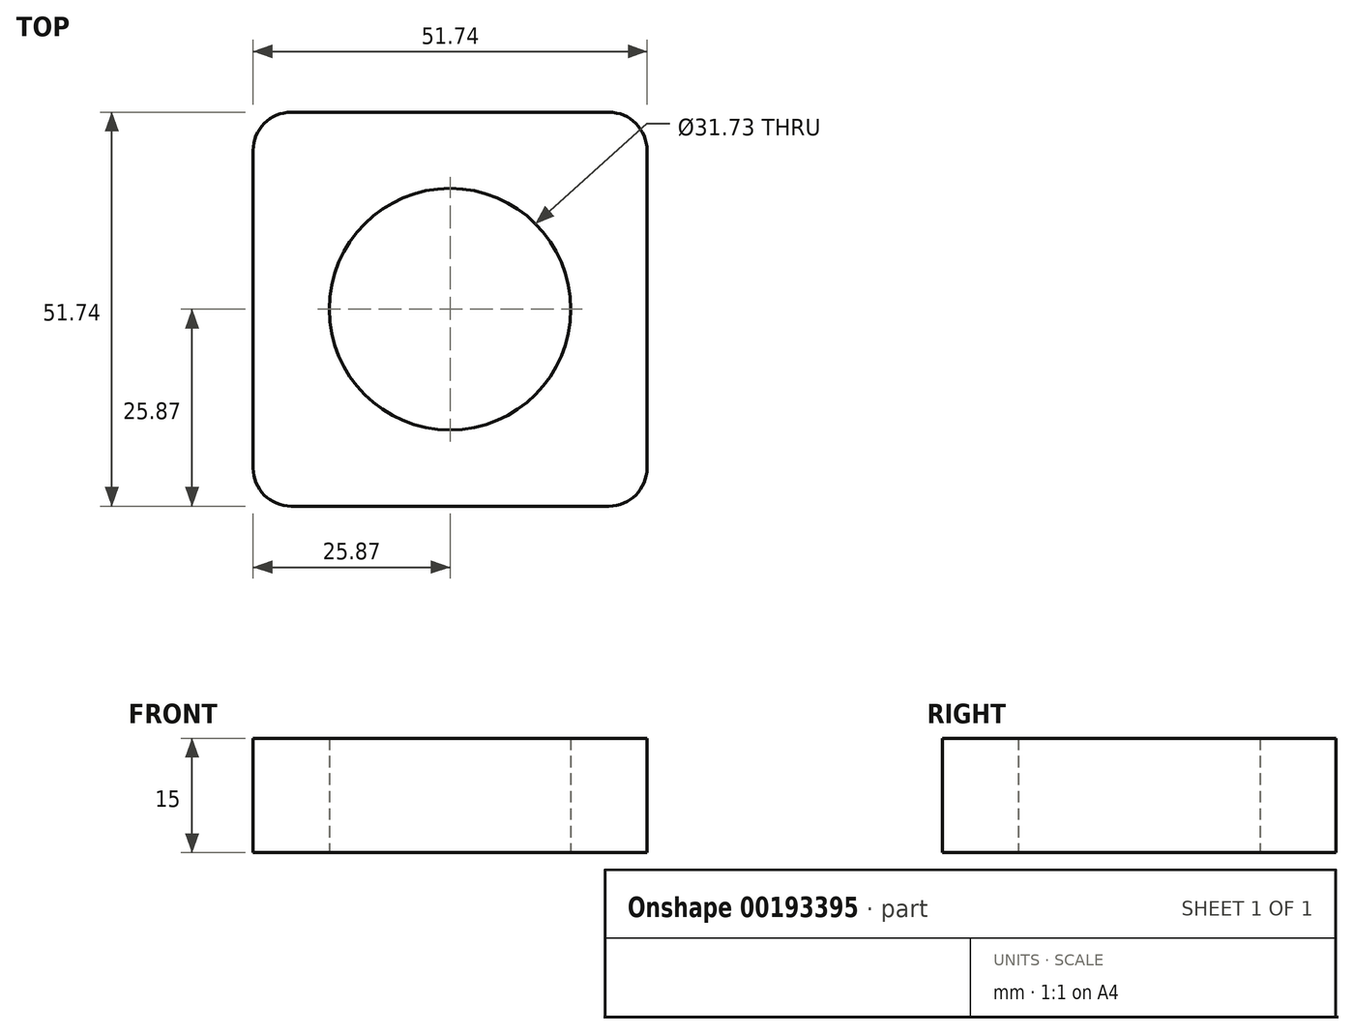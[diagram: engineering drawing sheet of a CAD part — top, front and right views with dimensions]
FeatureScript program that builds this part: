
annotation { "Feature Type Name" : "Feature", "Feature Type Description" : "" }
export const myFeature = defineFeature(function(context is Context, id is Id, definition is map)
    precondition{}
    {
        {
            var Q0;
            Q0=qCreatedBy(makeId("Top.planeOp"),FACE);
            var sketch = newSketch(context, id + "F0", { "sketchPlane" : qUnion([Q0])});
            skLineSegment(sketch, "E0.bottom", {"start": v(-25.87, 25.86) * mm, "end": v(25.86, 25.86) * mm});
            skLineSegment(sketch, "E0.top", {"start": v(-25.86, -25.86) * mm, "end": v(25.86, -25.86) * mm});
            skLineSegment(sketch, "E0.left", {"start": v(-25.87, 25.86) * mm, "end": v(-25.86, -25.86) * mm});
            skLineSegment(sketch, "E0.right", {"start": v(25.86, 25.86) * mm, "end": v(25.86, -25.86) * mm});
            skCircle(sketch, "E1", {"center": v(0, 0) * mm, "radius": 15.87 * mm});
            skSolve(sketch);
        }
        {
            var Q0;
            Q0=makeQuery(id+"F0.imprint","IMPRINT",FACE,{"disambiguationData":[TD([[makeQuery(id+"F0.imprint","IMPRINT",EDGE,{"derivedFrom":sQuery(id+"F0.wireOp",EDGE,"E0.bottom")}),-1.0]])]});
            extrude(context, id + "F1", {"entities" : qUnion([Q0]), "depth" : 15 * mm});
        }
        {
            var Q0;
            Q0=makeQuery(id+"F1.opExtrude","SWEPT_EDGE",EDGE,{"disambiguationData":[OSD([sQuery(id+"F0.wireOp",EDGE,"E0.top"),sQuery(id+"F0.wireOp",EDGE,"E0.left")])]});
            var Q1;
            Q1=makeQuery(id+"F1.opExtrude","SWEPT_EDGE",EDGE,{"disambiguationData":[OSD([sQuery(id+"F0.wireOp",EDGE,"E0.top"),sQuery(id+"F0.wireOp",EDGE,"E0.right")])]});
            var Q2;
            Q2=makeQuery(id+"F1.opExtrude","SWEPT_EDGE",EDGE,{"disambiguationData":[OSD([sQuery(id+"F0.wireOp",EDGE,"E0.bottom"),sQuery(id+"F0.wireOp",EDGE,"E0.right")])]});
            var Q3;
            Q3=makeQuery(id+"F1.opExtrude","SWEPT_EDGE",EDGE,{"disambiguationData":[OSD([sQuery(id+"F0.wireOp",EDGE,"E0.bottom"),sQuery(id+"F0.wireOp",EDGE,"E0.left")])]});
            fillet(context, id + "F2", {"entities" : qUnion([Q0, Q1, Q2, Q3]), "radius" : 5 * mm, "tangentPropagation" : true, "allowEdgeOverflow" : false});
        }
    });
